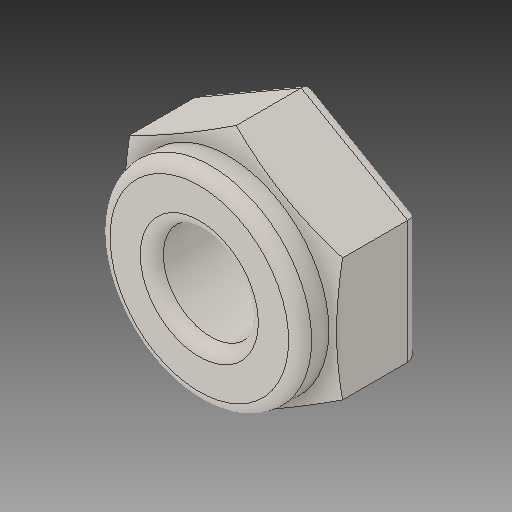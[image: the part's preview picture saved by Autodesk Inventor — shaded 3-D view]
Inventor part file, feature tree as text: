
AUTODESK INVENTOR PART (.ipt)
format: ipt  version: 2017 (Build 210142000, 142)  size: 164,864 bytes
history: native  units: in
note: dims shown in document units (in); Inventor stores cm internally (conversion verified against a paired STEP export)
features: fillet x1
ambient origin geometry x8: Origin, YZ Plane, XZ Plane, XY Plane, X Axis, Y Axis, Z Axis, Center Point
bodies: Solid1 (feature_tree)
feature tree (1):
  fillet  "Fillet4"  [1 undecoded]
note: 1 required parameter value undecoded (feature->parameter linkage not recoverable at this tier; creation-order binding heuristic only, values carry confidence <= 0.55)
